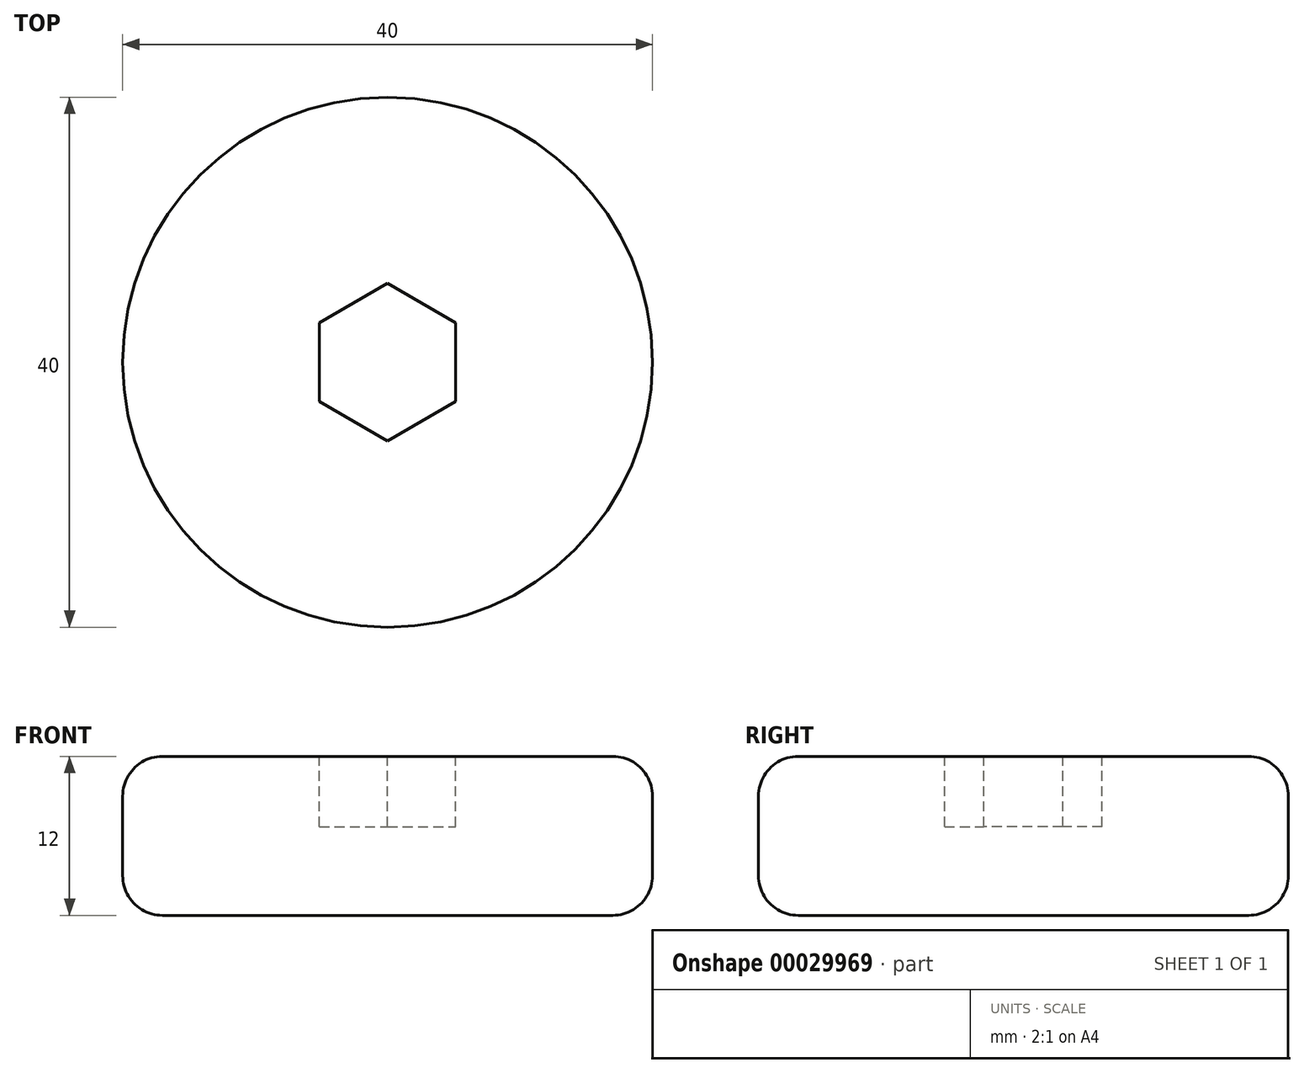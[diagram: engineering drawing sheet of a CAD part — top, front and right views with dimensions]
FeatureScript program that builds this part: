
annotation { "Feature Type Name" : "Feature", "Feature Type Description" : "" }
export const myFeature = defineFeature(function(context is Context, id is Id, definition is map)
    precondition{}
    {
        {
            var Q0;
            Q0=qCreatedBy(makeId("Top.planeOp"),FACE);
            var sketch = newSketch(context, id + "F0", { "sketchPlane" : qUnion([Q0])});
            skCircle(sketch, "E0", {"center": v(0, 0) * mm, "radius": 20 * mm});
            skSolve(sketch);
        }
        {
            var Q0;
            Q0 = qSketchRegion(id + "F0", true);
            extrude(context, id + "F1", {"entities" : qUnion([Q0]), "depth" : 12 * mm});
        }
        {
            var Q0;
            Q0=makeQuery(id+"F1.opExtrude","CAP_FACE",FACE,{"disambiguationData":[OSD([sQuery(id+"F0.wireOp",EDGE,"E0")])],"isStart":false});
            var sketch = newSketch(context, id + "F2", { "sketchPlane" : qUnion([Q0])});
            skCircle(sketch, "E1.cCircle", {"center": v(0, 0) * mm, "radius": 5.15 * mm, "construction": true});
            skLineSegment(sketch, "E1.0", {"start": v(5.15, 2.97) * mm, "end": v(5.15, -2.97) * mm});
            skLineSegment(sketch, "E1.1", {"start": v(5.15, -2.97) * mm, "end": v(0, -5.95) * mm});
            skLineSegment(sketch, "E1.2", {"start": v(0, -5.95) * mm, "end": v(-5.15, -2.97) * mm});
            skLineSegment(sketch, "E1.3", {"start": v(-5.15, -2.97) * mm, "end": v(-5.15, 2.97) * mm});
            skLineSegment(sketch, "E1.4", {"start": v(-5.15, 2.97) * mm, "end": v(0, 5.95) * mm});
            skLineSegment(sketch, "E1.5", {"start": v(0, 5.95) * mm, "end": v(5.15, 2.97) * mm});
            skPoint(sketch, "E1.0.midPoint", {"position": v(5.15, 0) * mm});
            skSolve(sketch);
        }
        {
            var Q0;
            Q0 = qSketchRegion(id + "F2", true);
            extrude(context, id + "F3", {"entities" : qUnion([Q0]), "operationType" : NewBodyOperationType.REMOVE, "oppositeDirection" : true, "depth" : 5.3 * mm});
        }
        {
            var Q0;
            Q0=makeQuery(id+"F1.opExtrude","CAP_EDGE",EDGE,{"disambiguationData":[OSD([sQuery(id+"F0.wireOp",EDGE,"E0")])],"isStart":false});
            var Q1;
            Q1=makeQuery(id+"F1.opExtrude","CAP_EDGE",EDGE,{"disambiguationData":[OSD([sQuery(id+"F0.wireOp",EDGE,"E0")])],"isStart":true});
            fillet(context, id + "F4", {"entities" : qUnion([Q0, Q1]), "radius" : 3 * mm, "tangentPropagation" : true, "allowEdgeOverflow" : false});
        }
    });
